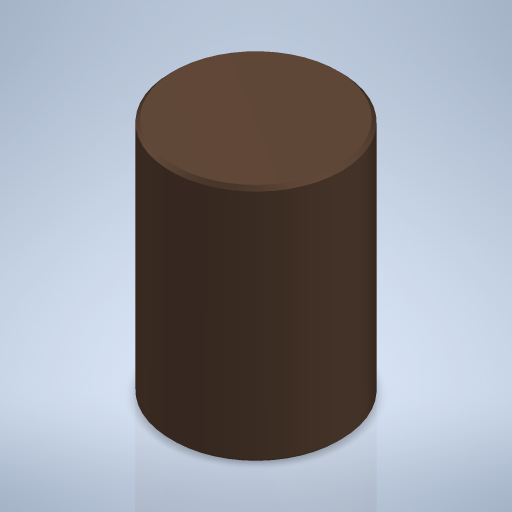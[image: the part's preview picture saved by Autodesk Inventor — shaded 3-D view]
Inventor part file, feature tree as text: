
AUTODESK INVENTOR PART (.ipt)
format: ipt  version: 2024 (Build 280153000, 153)  size: 231,424 bytes
history: native  units: mm
features: sketch x3, extrude x2, plane x1, hole x1, chamfer x1
ambient origin geometry x8: Origin, YZ Plane, XZ Plane, XY Plane, X Axis, Y Axis, Z Axis, Center Point
bodies: Volumenkörper1 (feature_tree)
feature tree (8):
  extrude  "Extrusion1"  Depth=14.0mm TaperAngle=0.0deg
  extrude  "Extrusion2"  Depth=7.5mm TaperAngle=0.0deg
  plane  "Arbeitsebene1"
  hole  "Bohrung1"  [1 undecoded]
  chamfer  "Fasen1"  [1 undecoded]
  sketch  "Skizze1"  dims[d0=10.0mm d1=14.0mm d2=0.0mm]
  sketch  "Skizze2"  dims[d3=8.0mm d4=7.5mm d5=0.0mm]
  sketch  "Skizze3"  dims[d6=7.5mm d7=1.5mm d8=6.0mm d9=4.0mm d10=2.0mm d11=90.0deg d12=4.5mm d13=20.594885mm d14=0.2mm d15=2.0mm d16=45.0deg]
note: 2 required parameter values undecoded (feature->parameter linkage not recoverable at this tier; creation-order binding heuristic only, values carry confidence <= 0.55)
